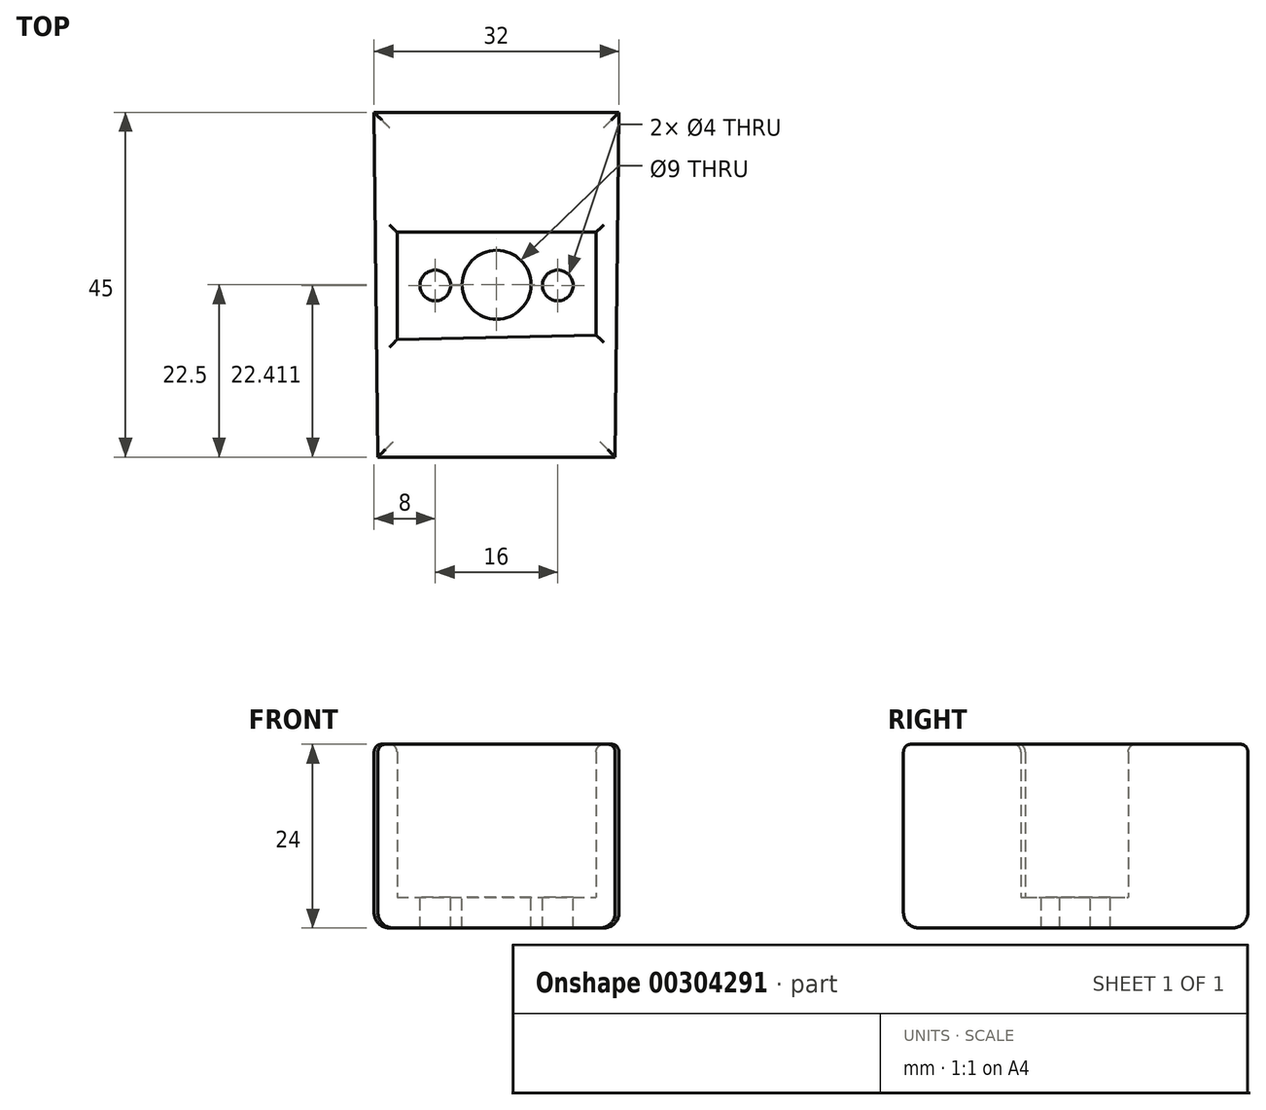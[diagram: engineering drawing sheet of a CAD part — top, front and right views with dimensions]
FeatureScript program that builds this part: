
annotation { "Feature Type Name" : "Feature", "Feature Type Description" : "" }
export const myFeature = defineFeature(function(context is Context, id is Id, definition is map)
    precondition{}
    {
        {
            var Q0;
            Q0=qCreatedBy(makeId("Top.planeOp"),FACE);
            var sketch = newSketch(context, id + "F0", { "sketchPlane" : qUnion([Q0])});
            skLineSegment(sketch, "E0", {"start": v(0, 0) * mm, "end": v(31, 0) * mm});
            skLineSegment(sketch, "E1", {"start": v(15.5, 0) * mm, "end": v(15.5, 45) * mm, "construction": true});
            skLineSegment(sketch, "E2", {"start": v(15.5, 45) * mm, "end": v(31.5, 45) * mm});
            skLineSegment(sketch, "E3.MirrorCS", {"start": v(15.5, 45) * mm, "end": v(-0.5, 45) * mm});
            skLineSegment(sketch, "E4", {"start": v(0, 0) * mm, "end": v(-0.5, 45) * mm});
            skLineSegment(sketch, "E5", {"start": v(31, 0) * mm, "end": v(31.5, 45) * mm});
            skLineSegment(sketch, "E6", {"start": v(15.5, 22.5) * mm, "end": v(31.25, 22.33) * mm, "construction": true});
            skLineSegment(sketch, "E7.MirrorCS", {"start": v(15.5, 22.5) * mm, "end": v(-0.25, 22.33) * mm, "construction": true});
            skLineSegment(sketch, "E8.0", {"start": v(2.5, 15.36) * mm, "end": v(2.5, 29.36) * mm});
            skLineSegment(sketch, "E9.MirrorCS", {"start": v(28.5, 15.93) * mm, "end": v(28.5, 29.36) * mm});
            skLineSegment(sketch, "E10.0", {"start": v(15.42, 29.5) * mm, "end": v(2.5, 29.36) * mm});
            skLineSegment(sketch, "E11.MirrorCS", {"start": v(15.58, 29.5) * mm, "end": v(28.5, 29.36) * mm});
            skLineSegment(sketch, "E12.MirrorCS", {"start": v(15.58, 15.5) * mm, "end": v(2.5, 15.36) * mm});
            skLineSegment(sketch, "E13.MirrorCS", {"start": v(15.73, 15.5) * mm, "end": v(28.5, 15.93) * mm});
            skPoint(sketch, "E14.orphan", {"position": v(-0.33, 29.32) * mm});
            skPoint(sketch, "E15.orphan", {"position": v(2.5, 45) * mm});
            skPoint(sketch, "E16.orphan", {"position": v(2.5, 0) * mm});
            skPoint(sketch, "E17.orphan", {"position": v(28.5, 0) * mm});
            skLineSegment(sketch, "E18.trimOffspring", {"start": v(31.18, 16.02) * mm, "end": v(31.47, 16.03) * mm});
            skPoint(sketch, "E19.orphan", {"position": v(31.33, 29.32) * mm});
            skPoint(sketch, "E20.orphan", {"position": v(28.5, 45) * mm});
            skPoint(sketch, "E21.orphan", {"position": v(-0.17, 15.33) * mm});
            skLineSegment(sketch, "E22", {"start": v(2.5, 15.36) * mm, "end": v(28.5, 15.93) * mm});
            skLineSegment(sketch, "E23", {"start": v(28.5, 29.36) * mm, "end": v(2.5, 29.36) * mm});
            skCircle(sketch, "E24", {"center": v(15.5, 22.5) * mm, "radius": 4.5 * mm});
            skCircle(sketch, "E25", {"center": v(23.5, 22.41) * mm, "radius": 2 * mm});
            skCircle(sketch, "E26.MirrorC", {"center": v(7.5, 22.41) * mm, "radius": 2 * mm});
            skSolve(sketch);
        }
        {
            var Q0;
            {var subQ1=sQuery(id+"F0.wireOp",EDGE,"E0");Q0=makeQuery(id+"F0.imprint","IMPRINT",FACE,{"disambiguationData":[TD([[makeQuery(id+"F0.imprint","IMPRINT",EDGE,{"derivedFrom":subQ1}),1.0]])]});}
            extrude(context, id + "F1", {"entities" : qUnion([Q0]), "depth" : 20 * mm});
        }
        {
            var Q0;
            Q0=makeQuery(id+"F0.imprint","IMPRINT",FACE,{"disambiguationData":[TD([[makeQuery(id+"F0.imprint","IMPRINT",EDGE,{"derivedFrom":sQuery(id+"F0.wireOp",EDGE,"E8.0")}),-1.0]])]});
            var Q1;
            {var subQ1=sQuery(id+"F0.wireOp",EDGE,"E0");Q1=makeQuery(id+"F0.imprint","IMPRINT",FACE,{"disambiguationData":[TD([[makeQuery(id+"F0.imprint","IMPRINT",EDGE,{"derivedFrom":subQ1}),1.0]])]});}
            extrude(context, id + "F2", {"entities" : qUnion([Q0, Q1]), "operationType" : NewBodyOperationType.ADD, "oppositeDirection" : true, "depth" : 4 * mm});
        }
        {
            var Q0;
            Q0=makeQuery(id+"F2.opExtrude","CAP_EDGE",EDGE,{"disambiguationData":[OSD([sQuery(id+"F0.wireOp",EDGE,"E5")])],"isStart":false});
            var Q1;
            Q1=makeQuery(id+"F2.opExtrude","CAP_EDGE",EDGE,{"disambiguationData":[OSD([sQuery(id+"F0.wireOp",EDGE,"E0")])],"isStart":false});
            var Q2;
            Q2=makeQuery(id+"F2.opExtrude","CAP_EDGE",EDGE,{"disambiguationData":[OSD([sQuery(id+"F0.wireOp",EDGE,"E4")])],"isStart":false});
            var Q3;
            Q3=makeQuery(id+"F2.opExtrude","CAP_EDGE",EDGE,{"disambiguationData":[OSD([sQuery(id+"F0.wireOp",EDGE,"E2"),sQuery(id+"F0.wireOp",EDGE,"E3.MirrorCS")])],"isStart":false});
            fillet(context, id + "F3", {"entities" : qUnion([Q0, Q1, Q2, Q3]), "radius" : 2 * mm, "tangentPropagation" : true, "allowEdgeOverflow" : false});
        }
        {
            var Q0;
            Q0=makeQuery(id+"F1.opExtrude","CAP_EDGE",EDGE,{"disambiguationData":[OSD([sQuery(id+"F0.wireOp",EDGE,"E0")])],"isStart":false});
            var Q1;
            Q1=makeQuery(id+"F1.opExtrude","CAP_EDGE",EDGE,{"disambiguationData":[OSD([sQuery(id+"F0.wireOp",EDGE,"E5")])],"isStart":false});
            var Q2;
            Q2=makeQuery(id+"F1.opExtrude","CAP_FACE",FACE,{"disambiguationData":[OSD([sQuery(id+"F0.wireOp",EDGE,"E0"),sQuery(id+"F0.wireOp",EDGE,"E2"),sQuery(id+"F0.wireOp",EDGE,"E3.MirrorCS"),sQuery(id+"F0.wireOp",EDGE,"E4"),sQuery(id+"F0.wireOp",EDGE,"E5"),sQuery(id+"F0.wireOp",EDGE,"E8.0"),sQuery(id+"F0.wireOp",EDGE,"E9.MirrorCS"),sQuery(id+"F0.wireOp",EDGE,"E22"),sQuery(id+"F0.wireOp",EDGE,"E23")])],"isStart":false});
            var Q3;
            Q3=makeQuery(id+"F1.opExtrude","CAP_EDGE",EDGE,{"disambiguationData":[OSD([sQuery(id+"F0.wireOp",EDGE,"E9.MirrorCS")])],"isStart":true});
            var Q4;
            Q4=makeQuery(id+"F1.opExtrude","CAP_EDGE",EDGE,{"disambiguationData":[OSD([sQuery(id+"F0.wireOp",EDGE,"E22")])],"isStart":true});
            var Q5;
            Q5=makeQuery(id+"F1.opExtrude","CAP_EDGE",EDGE,{"disambiguationData":[OSD([sQuery(id+"F0.wireOp",EDGE,"E23")])],"isStart":true});
            var Q6;
            Q6=makeQuery(id+"F1.opExtrude","CAP_EDGE",EDGE,{"disambiguationData":[OSD([sQuery(id+"F0.wireOp",EDGE,"E8.0")])],"isStart":true});
            fillet(context, id + "F4", {"entities" : qUnion([Q0, Q1, Q2, Q3, Q4, Q5, Q6]), "radius" : 1 * mm, "tangentPropagation" : true, "allowEdgeOverflow" : false});
        }
    });
